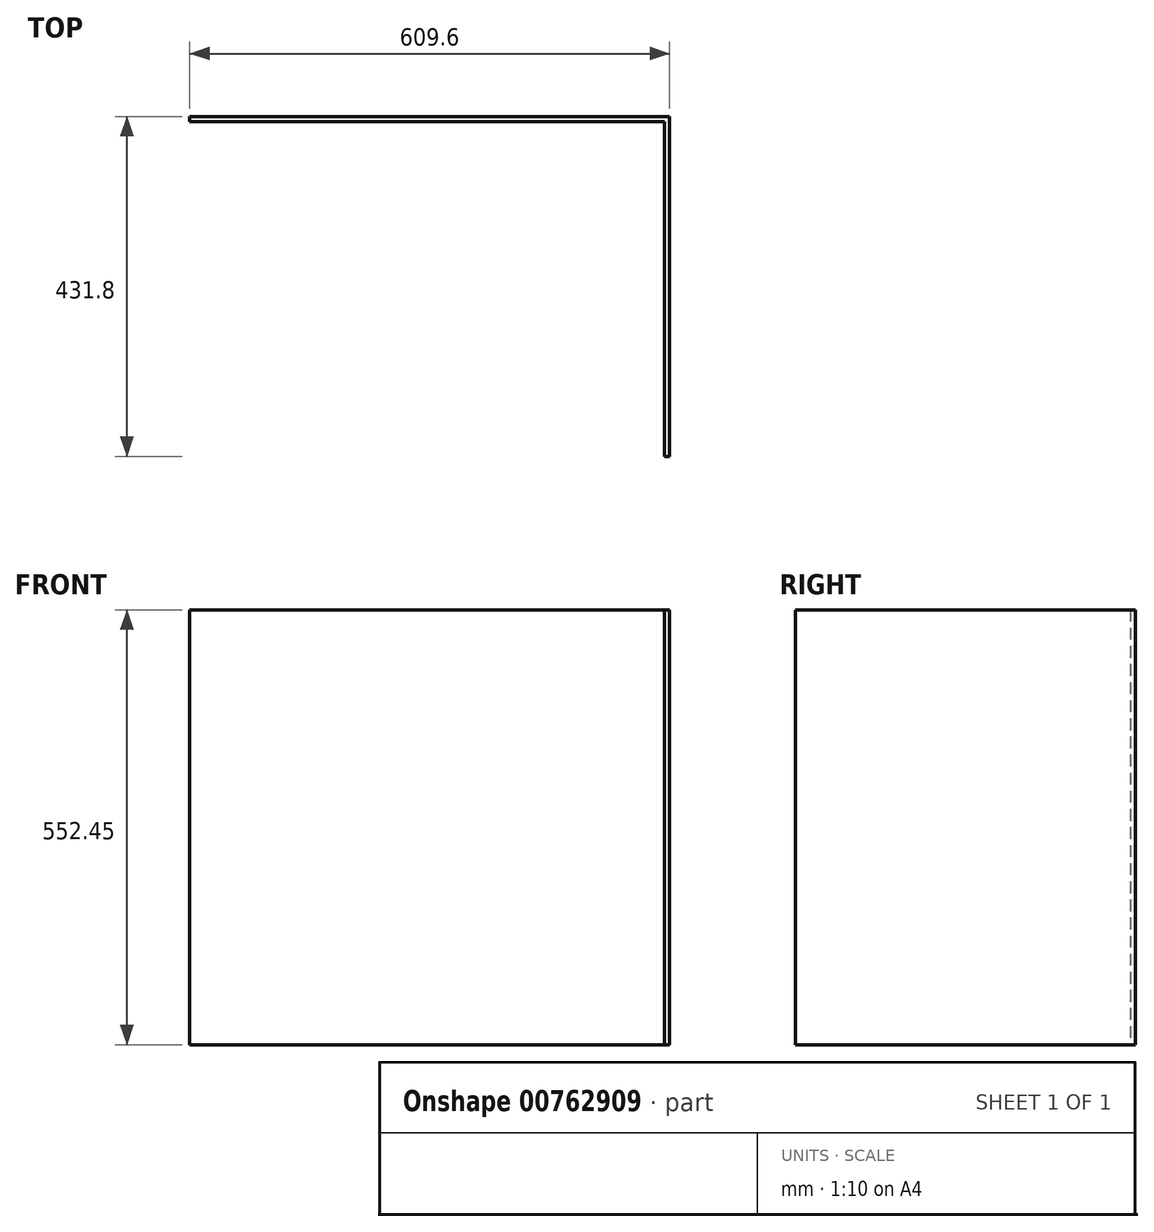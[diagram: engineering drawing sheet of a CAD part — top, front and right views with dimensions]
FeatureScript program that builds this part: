
annotation { "Feature Type Name" : "Feature", "Feature Type Description" : "" }
export const myFeature = defineFeature(function(context is Context, id is Id, definition is map)
    precondition{}
    {
        {
            var Q0;
            Q0=qCreatedBy(makeId("Top.planeOp"),FACE);
            var sketch = newSketch(context, id + "F0", { "sketchPlane" : qUnion([Q0])});
            skLineSegment(sketch, "E0", {"start": v(-609.6, 0) * mm, "end": v(0, 0) * mm});
            skLineSegment(sketch, "E1", {"start": v(0, 0) * mm, "end": v(0, -431.8) * mm});
            skLineSegment(sketch, "E2.0", {"start": v(-6.35, -6.35) * mm, "end": v(-6.35, -431.8) * mm});
            skLineSegment(sketch, "E2.1", {"start": v(-609.6, -6.35) * mm, "end": v(-6.35, -6.35) * mm});
            skLineSegment(sketch, "E3", {"start": v(-609.6, 0) * mm, "end": v(-609.6, -6.35) * mm});
            skLineSegment(sketch, "E4", {"start": v(-6.35, -431.8) * mm, "end": v(0, -431.8) * mm});
            skSolve(sketch);
        }
        {
            var Q0;
            Q0 = qSketchRegion(id + "F0", true);
            extrude(context, id + "F1", {"entities" : qUnion([Q0]), "depth" : 552.45 * mm, "offsetDistance" : 25.4 * mm});
        }
    });
